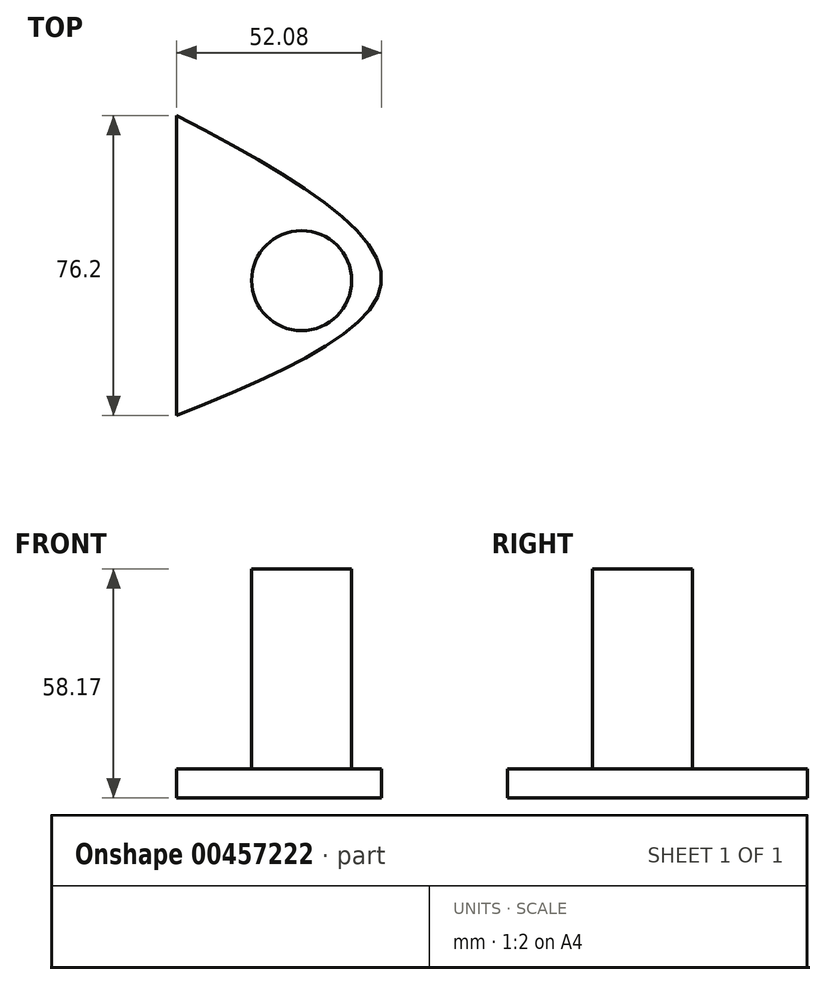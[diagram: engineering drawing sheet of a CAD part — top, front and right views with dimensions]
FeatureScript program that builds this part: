
annotation { "Feature Type Name" : "Feature", "Feature Type Description" : "" }
export const myFeature = defineFeature(function(context is Context, id is Id, definition is map)
    precondition{}
    {
        {
            var Q0;
            Q0=qCreatedBy(makeId("Top.planeOp"),FACE);
            var sketch = newSketch(context, id + "F0", { "sketchPlane" : qUnion([Q0])});
            skLineSegment(sketch, "E0", {"start": v(-31.75, 41.92) * mm, "end": v(-31.75, -34.28) * mm});
            skFitSpline(sketch, "E1", {"points": [v(-31.75, 41.92) * mm, v(20.32, 0) * mm, v(-31.75, -34.28) * mm], "startDerivative": vector(166.51, -85.8) * mm, "endDerivative": vector(-168.3, -66.5) * mm});
            skCircle(sketch, "E2", {"center": v(0, 0) * mm, "radius": 12.7 * mm});
            skSolve(sketch);
        }
        {
            var Q0;
            Q0=makeQuery(id+"F0.imprint","IMPRINT",FACE,{"disambiguationData":[TD([[makeQuery(id+"F0.imprint","IMPRINT",EDGE,{"derivedFrom":sQuery(id+"F0.wireOp",EDGE,"E2")}),1.0]])]});
            extrude(context, id + "F1", {"entities" : qUnion([Q0]), "depth" : 50.8 * mm});
        }
        {
            var Q0;
            Q0=makeQuery(id+"F0.imprint","IMPRINT",FACE,{"disambiguationData":[TD([[makeQuery(id+"F0.imprint","IMPRINT",EDGE,{"derivedFrom":sQuery(id+"F0.wireOp",EDGE,"E0")}),1.0]])]});
            var Q1;
            Q1=makeQuery(id+"F0.imprint","IMPRINT",FACE,{"disambiguationData":[TD([[makeQuery(id+"F0.imprint","IMPRINT",EDGE,{"derivedFrom":sQuery(id+"F0.wireOp",EDGE,"E2")}),1.0]])]});
            extrude(context, id + "F2", {"entities" : qUnion([Q0, Q1]), "operationType" : NewBodyOperationType.ADD, "oppositeDirection" : true, "depth" : 7.37 * mm});
        }
    });
